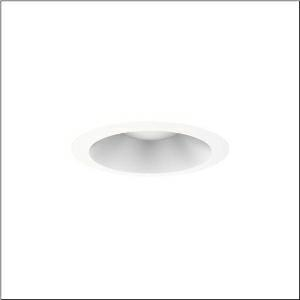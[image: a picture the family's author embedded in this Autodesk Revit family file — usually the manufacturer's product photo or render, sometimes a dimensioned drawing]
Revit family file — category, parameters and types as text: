
# Revit family: lunis_31_midi_51dn15dg32
name_source: partatom
category: Lighting Fixtures
units: mm (PartAtom-declared; Revit-internal decimal feet)

## family parameters
Cut with Voids When Loaded = No
Host = Face
Light Source = No
Part Type = Normal
Room Calculation Point = No
Round Connector Dimension = Use Diameter
Shared = No

## types (1)
- Lunis 31 midi (1 x LED, 2000 lm, 17 W, 3000K)
    Apparent Load = 17 VA
    CIE Flux Codes = 89 99 100 100 100
    Color Rendering = 80
    Color Temperature = 3000K
    Default Elevation = 1800 mm
    Description = Lunis 31,  midi, downlight, light control with reflector, light emission: direct distribution, LED rated luminous flux: 2.050lm, light colour: 830, control gear: ECG DALI, mains connection: 220..240V, AC, 50/60Hz, housing, white, protection rating (complete): IP20, insulation class (complete): insulation class II (safety insulation), certification: CE, packaging unit: 1 piece
    Height = 0 mm  [stored 0 ft]
    Lamp = 1 x LED
    Lamp Light Flux = 2000 lm
    Lamp Power = 17 W
    Lamp count = 1
    Length = 259 mm
    Luminous efficacy = 118 lm/W
    Manufacturer = Siteco
    ModVariant = No
    Model = 51DN15DG32
    Mounting Place = Ceiling
    Mounting Type = Recessed
    Number of Poles = 1
    OnlyDefault = Yes
    Power Factor = 1
    Product Name = Lunis 31 midi
    Product group = downlight | ceiling recessed
    ProductGroupID = 402
    Protection Class = Protection class II
    Protection Degree = IP 20
    RLX_Detail_Level = 1
    RlxData = <blob elided: 23733 chars, md5=c7dad706>
    Socket = socket
    Standby Power = 0 W
    System Light Flux = 2000 lm
    System Power = 17 W
    Type Comments = Product without accessories
    Type Image = l_1006711.jpg
    URL = http://relux.com
    VarID = ---
    Voltage = 0 V
    Weight = 0.00 kg
    Width = 0 mm  [stored 0 ft]

note: [stored X ft] marks values corroborated as IEEE doubles in the binary element streams (Revit-internal decimal feet)

## geometry (parser evidence)
native form markers: Blend x4, Sweep x11
no freeform markers — native parametric forms only
